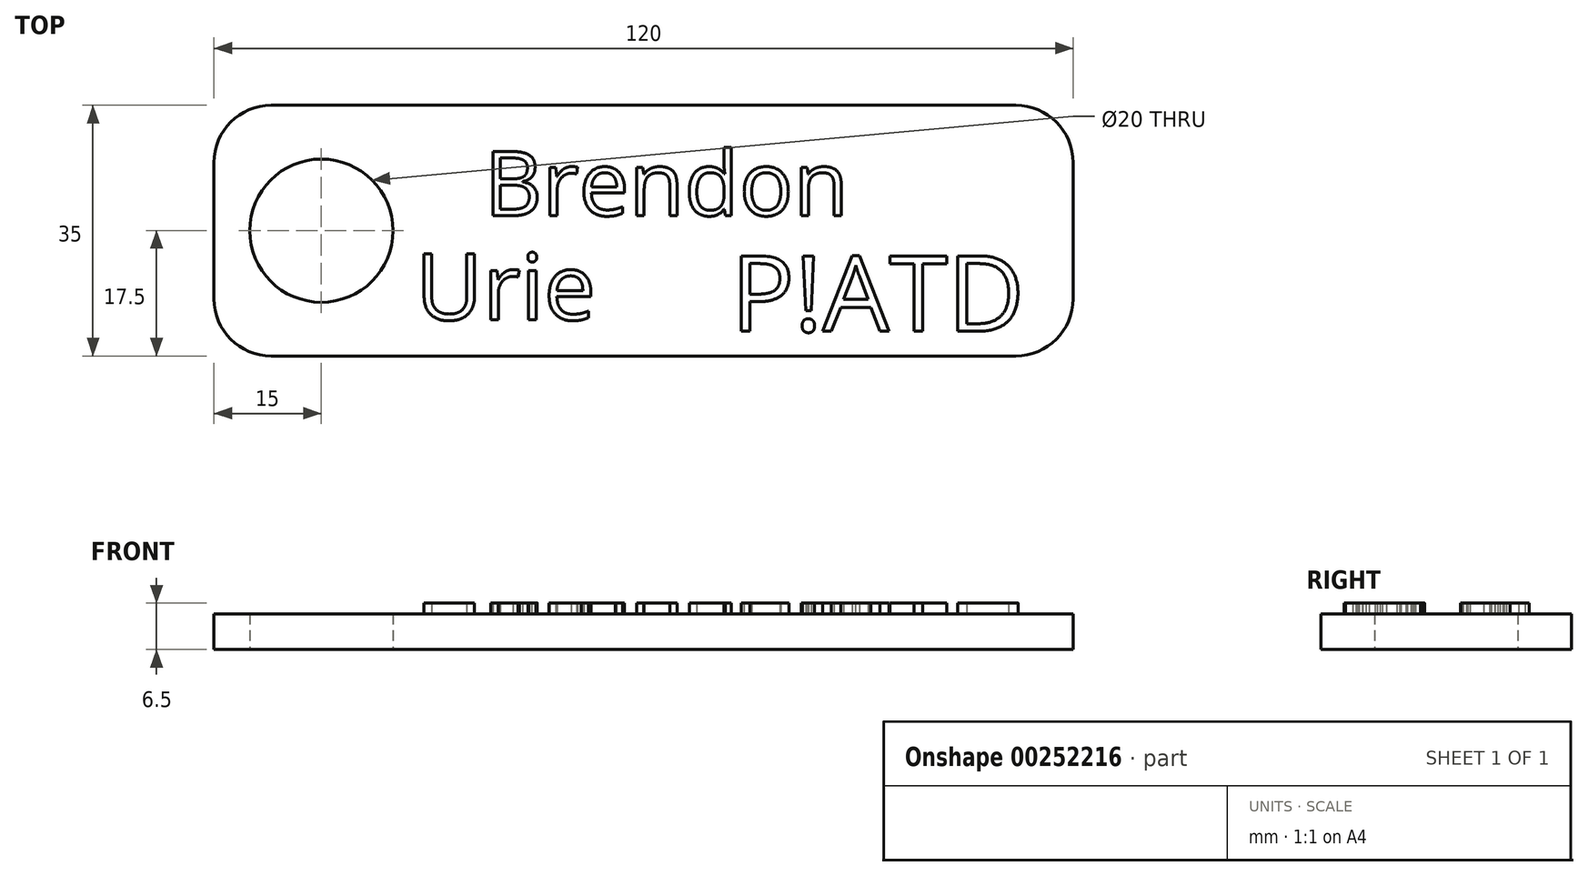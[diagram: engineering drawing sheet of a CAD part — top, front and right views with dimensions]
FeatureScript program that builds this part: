
annotation { "Feature Type Name" : "Feature", "Feature Type Description" : "" }
export const myFeature = defineFeature(function(context is Context, id is Id, definition is map)
    precondition{}
    {
        {
            var Q0;
            Q0=qCreatedBy(makeId("Top.planeOp"),FACE);
            var sketch = newSketch(context, id + "F0", { "sketchPlane" : qUnion([Q0])});
            skLineSegment(sketch, "E0.bottom", {"start": v(-60, 17.5) * mm, "end": v(60, 17.5) * mm});
            skLineSegment(sketch, "E0.top", {"start": v(-60, -17.5) * mm, "end": v(60, -17.5) * mm});
            skLineSegment(sketch, "E0.left", {"start": v(-60, 17.5) * mm, "end": v(-60, -17.5) * mm});
            skLineSegment(sketch, "E0.right", {"start": v(60, 17.5) * mm, "end": v(60, -17.5) * mm});
            skPoint(sketch, "E0.middle", {"position": v(0, 0) * mm});
            skCircle(sketch, "E1", {"center": v(-45, 0) * mm, "radius": 10 * mm});
            skSolve(sketch);
        }
        {
            var Q0;
            Q0=makeQuery(id+"F0.imprint","IMPRINT",FACE,{"disambiguationData":[TD([[makeQuery(id+"F0.imprint","IMPRINT",EDGE,{"derivedFrom":sQuery(id+"F0.wireOp",EDGE,"E0.bottom")}),-1.0]])]});
            extrude(context, id + "F1", {"entities" : qUnion([Q0]), "depth" : 5 * mm});
        }
        {
            var Q0;
            Q0=makeQuery(id+"F1.opExtrude","SWEPT_EDGE",EDGE,{"disambiguationData":[OSD([sQuery(id+"F0.wireOp",EDGE,"E0.bottom"),sQuery(id+"F0.wireOp",EDGE,"E0.left")])]});
            var Q1;
            Q1=makeQuery(id+"F1.opExtrude","SWEPT_EDGE",EDGE,{"disambiguationData":[OSD([sQuery(id+"F0.wireOp",EDGE,"E0.bottom"),sQuery(id+"F0.wireOp",EDGE,"E0.right")])]});
            var Q2;
            Q2=makeQuery(id+"F1.opExtrude","SWEPT_EDGE",EDGE,{"disambiguationData":[OSD([sQuery(id+"F0.wireOp",EDGE,"E0.top"),sQuery(id+"F0.wireOp",EDGE,"E0.right")])]});
            var Q3;
            Q3=makeQuery(id+"F1.opExtrude","SWEPT_EDGE",EDGE,{"disambiguationData":[OSD([sQuery(id+"F0.wireOp",EDGE,"E0.top"),sQuery(id+"F0.wireOp",EDGE,"E0.left")])]});
            fillet(context, id + "F2", {"entities" : qUnion([Q0, Q1, Q2, Q3]), "radius" : 8 * mm, "tangentPropagation" : true, "allowEdgeOverflow" : false});
        }
        {
            var Q0;
            Q0=makeQuery(id+"F1.opExtrude","CAP_FACE",FACE,{"disambiguationData":[OSD([sQuery(id+"F0.wireOp",EDGE,"E0.bottom"),sQuery(id+"F0.wireOp",EDGE,"E0.top"),sQuery(id+"F0.wireOp",EDGE,"E0.left"),sQuery(id+"F0.wireOp",EDGE,"E0.right"),sQuery(id+"F0.wireOp",EDGE,"E1")])],"isStart":false});
            var sketch = newSketch(context, id + "F3", { "sketchPlane" : qUnion([Q0])});
            skSolve(sketch);
        }
        {
            var Q0;
            {var subQ0=sQuery(id+"F0.wireOp",EDGE,"E1");Q0=makeQuery(id+"F3.imprint","IMPRINT",FACE,{"disambiguationData":[TD([[makeQuery(id+"F3.imprint","IMPRINT",EDGE,{"derivedFrom":makeQuery(id+"F1.opExtrude","CAP_EDGE",EDGE,{"disambiguationData":[OSD([subQ0])],"isStart":false})}),-1.0]])]});}
            var sketch = newSketch(context, id + "F4", { "sketchPlane" : qUnion([Q0])});
            skText(sketch, "E2", { "text": "Brendon", "fontName": "OpenSans-Regular.ttf"});
            skText(sketch, "E3", { "text": "Urie", "fontName": "OpenSans-Regular.ttf"});
            skText(sketch, "E4", { "text": "P!ATD", "fontName": "OpenSans-Regular.ttf"});
            const initialGuessF4  = {"E2": [-0.02227, 0.00212, 1, 0, 0.00902], "E3": [-0.03182, -0.01246, 1, 0, 0.00928], "E4": [0.0122, -0.01405, 1, 0, 0.0106]};
            skSetInitialGuess(sketch, initialGuessF4);
            skSolve(sketch);
        }
        {
            var Q0;
            Q0 = qSketchRegion(id + "F4", true);
            extrude(context, id + "F5", {"entities" : qUnion([Q0]), "operationType" : NewBodyOperationType.ADD, "depth" : 1.5 * mm});
        }
    });
